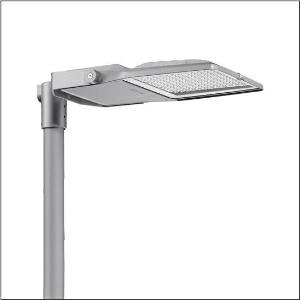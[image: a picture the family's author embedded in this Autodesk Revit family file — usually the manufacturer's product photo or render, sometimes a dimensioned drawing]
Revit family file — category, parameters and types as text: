
# Revit family: floodlight_fl_21_midi___pl61_5xa7785e2c3a_8e59
name_source: partatom
category: Lighting Fixtures
units: mm (PartAtom-declared; Revit-internal decimal feet)

## family parameters
Cut with Voids When Loaded = No
Host = Face
Light Source = No
Part Type = Normal
Room Calculation Point = No
Round Connector Dimension = Use Diameter
Shared = No

## types (1)
- --- (1 x LED, 26450 lm, 212.4 W, 3000K)
    Apparent Load = 212 VA
    CIE Flux Codes = 33 65 98 100 100
    Color Rendering = 70
    Color Temperature = 3000K
    Default Elevation = 1800 mm
    Description = Floodlight FL 21 midi, floodlight, primary light control with lens, of PMMA, primary optical cover: protective disc, of toughened safety glass, transparent, light distribution: PL61, light emission: direct distribution, installation type: surface-mounted, LED, High Power LED, rated luminous flux: 26.450lm, luminous efficacy: 125lm/W, light colour: 730, colour temperature: 3000K, control gear: ECG Smart Interface, control: flexible luminous flux parameterisation, time-dependent luminous flux control, constant luminous flux control, overheat protection, pre-setting: logarithmic dimming characteristic, with terminal, 6-pole, mains connection: 220..240V, AC, 50/60Hz, start of lifetime: 212W, end of service life: 231W, reduction: 95W, luminaire housing, of diecast aluminium, powder-coated, Siteco® metallic grey (DB 702S), sealing non-destructively replaceable, please order mast flange separately, mast bracket, of steel, galvanised, powder-coated, Siteco® metallic grey (DB 702S), Smart Interface above, protection rating (complete): IP66, insulation class (complete): insulation class II (safety insulation), certification: CE, ENEC, VDE, protection symbol: D, impact resistance: IK08, permissible operating ambient temperature: -20..+40°C, permissible operating ambient temperature for outdoor applications: -40..+50°C, standard: DIN EN 12944, LABS conformity tested according to VDMA 24364:2018-05, packaging unit: 1 piece

Light Distribution: PL61
    Height = 76 mm
    Lamp = 1 x LED
    Lamp Light Flux = 26450 lm
    Lamp Power = 212.4 W
    Lamp count = 1
    Length = 657 mm
    Luminous efficacy = 125 lm/W
    Manufacturer = Siteco
    ModVariant = No
    Model = 5XA7785E2C3A
    Number of Poles = 1
    OnlyDefault = Yes
    Power Factor = 1
    Product Name = Floodlight FL 21 midi | PL61
    Product group = floodlight | pylon annexe
    ProductGroupID = 6200
    Protection Class = Protection class II
    Protection Degree = IP 66
    RLX_Detail_Level = 1
    RLX_Emergency_Light_Flux = 0 lm
    RLX_Emergency_Type = 0
    RLX_Emergency_Type_DB = No
    RlxData = <blob elided: 153469 chars, md5=ad262290>
    Socket = socket
    Standby Power = 0 W
    System Light Flux = 26450 lm
    System Power = 212 W
    Type Comments = factory setting: luminous flux: 100 % | dim-lin: 254 | 710 mA
    Type Image = l_1007123.jpg
    URL = http://relux.com
    VarID = @adj_166837
    Voltage = 0 V
    Weight = 0.00 kg
    Width = 442 mm

## geometry (parser evidence)
native form markers: Blend x4, Sweep x13
no freeform markers — native parametric forms only
